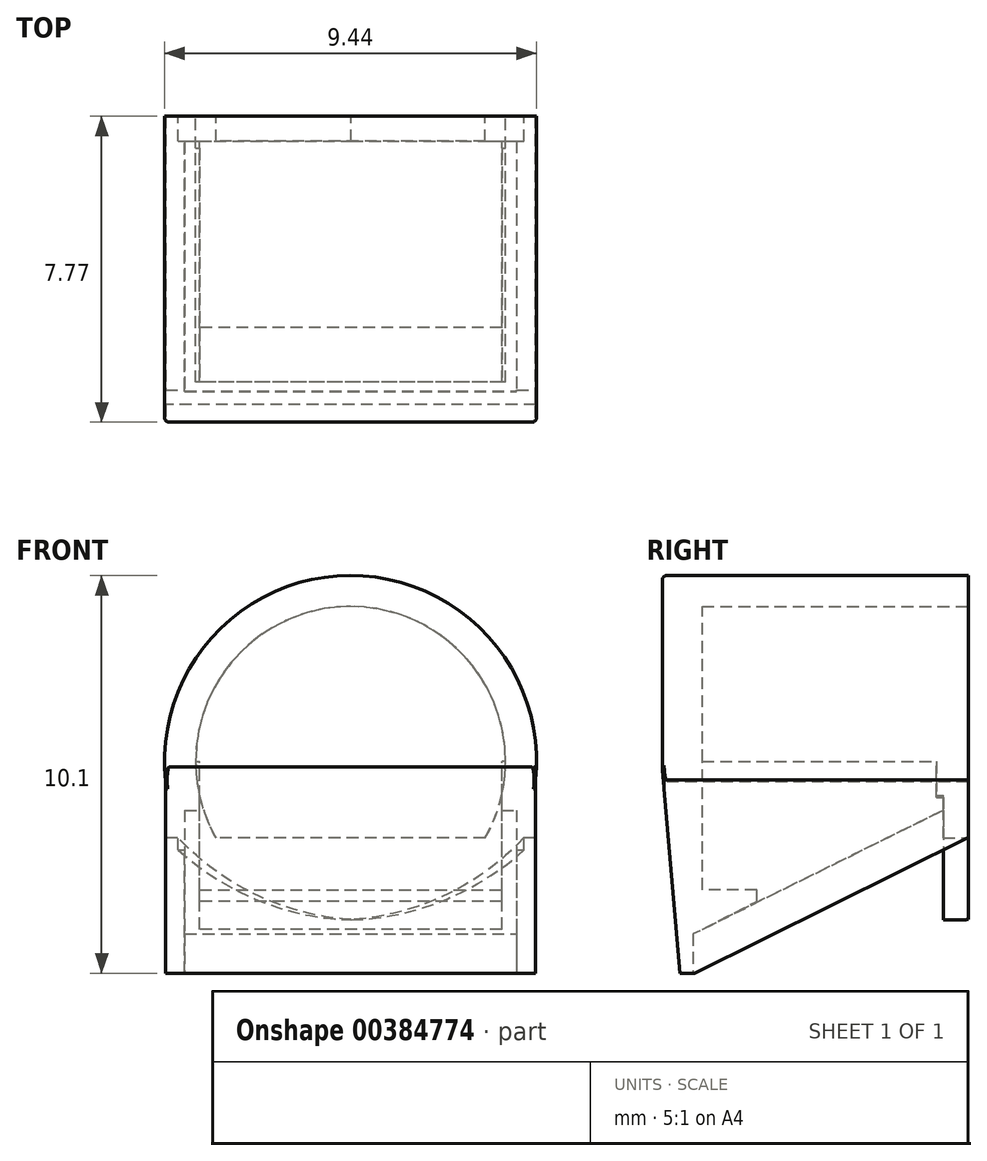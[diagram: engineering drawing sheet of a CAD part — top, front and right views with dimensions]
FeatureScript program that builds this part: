
annotation { "Feature Type Name" : "Feature", "Feature Type Description" : "" }
export const myFeature = defineFeature(function(context is Context, id is Id, definition is map)
    precondition{}
    {
        {
            var Q0;
            Q0=qCreatedBy(makeId("Front.planeOp"),FACE);
            var sketch = newSketch(context, id + "F0", { "sketchPlane" : qUnion([Q0])});
            skCircle(sketch, "E0", {"center": v(0, 0) * mm, "radius": 4.72 * mm});
            skSolve(sketch);
        }
        {
            var Q0;
            Q0=qCreatedBy(makeId("Front.planeOp"),FACE);
            var sketch = newSketch(context, id + "F1", { "sketchPlane" : qUnion([Q0])});
            skCircle(sketch, "E1", {"center": v(0, 0) * mm, "radius": 3.94 * mm});
            skSolve(sketch);
        }
        {
            var Q0;
            Q0=makeQuery(id+"F0.imprint","IMPRINT",FACE,{"disambiguationData":[TD([[makeQuery(id+"F0.imprint","IMPRINT",EDGE,{"derivedFrom":sQuery(id+"F0.wireOp",EDGE,"E0")}),1.0]])]});
            extrude(context, id + "F2", {"entities" : qUnion([Q0]), "depth" : 7.77 * mm});
        }
        {
            var Q0;
            Q0=makeQuery(id+"F1.imprint","IMPRINT",FACE,{"disambiguationData":[TD([[makeQuery(id+"F1.imprint","IMPRINT",EDGE,{"derivedFrom":sQuery(id+"F1.wireOp",EDGE,"E1")}),1.0]])]});
            extrude(context, id + "F3", {"entities" : qUnion([Q0]), "operationType" : NewBodyOperationType.REMOVE, "depth" : 6.76 * mm});
        }
        {
            var Q0;
            Q0=qCreatedBy(makeId("Top.planeOp"),FACE);
            var sketch = newSketch(context, id + "F4", { "sketchPlane" : qUnion([Q0])});
            skLineSegment(sketch, "E2.bottom", {"start": v(3.84, 0) * mm, "end": v(-3.83, 0) * mm});
            skLineSegment(sketch, "E2.top", {"start": v(3.84, -6.76) * mm, "end": v(-3.83, -6.76) * mm});
            skLineSegment(sketch, "E2.left", {"start": v(3.84, 0) * mm, "end": v(3.84, -6.76) * mm});
            skLineSegment(sketch, "E2.right", {"start": v(-3.83, 0) * mm, "end": v(-3.83, -6.76) * mm});
            skSolve(sketch);
        }
        {
            var Q0;
            Q0=qCreatedBy(makeId("Top.planeOp"),FACE);
            var sketch = newSketch(context, id + "F5", { "sketchPlane" : qUnion([Q0])});
            skLineSegment(sketch, "E3.bottom", {"start": v(-4.7, -7.73) * mm, "end": v(4.7, -7.73) * mm});
            skLineSegment(sketch, "E3.top", {"start": v(-4.7, 0) * mm, "end": v(4.7, 0) * mm});
            skLineSegment(sketch, "E3.left", {"start": v(-4.7, -7.73) * mm, "end": v(-4.7, 0) * mm});
            skLineSegment(sketch, "E3.right", {"start": v(4.7, -7.73) * mm, "end": v(4.7, 0) * mm});
            skSolve(sketch);
        }
        {
            var Q0;
            Q0=makeQuery(id+"F5.imprint","IMPRINT",FACE,{"disambiguationData":[TD([[makeQuery(id+"F5.imprint","IMPRINT",EDGE,{"derivedFrom":sQuery(id+"F5.wireOp",EDGE,"E3.bottom")}),1.0]])]});
            extrude(context, id + "F6", {"entities" : qUnion([Q0]), "operationType" : NewBodyOperationType.ADD, "oppositeDirection" : true, "depth" : 5.38 * mm});
        }
        {
            var Q0;
            Q0=makeQuery(id+"F4.imprint","IMPRINT",FACE,{"disambiguationData":[TD([[makeQuery(id+"F4.imprint","IMPRINT",EDGE,{"derivedFrom":sQuery(id+"F4.wireOp",EDGE,"E2.bottom")}),1.0]])]});
            extrude(context, id + "F7", {"entities" : qUnion([Q0]), "operationType" : NewBodyOperationType.REMOVE, "oppositeDirection" : true, "depth" : 11.68 * mm});
        }
        {
            var Q0;
            Q0=qCreatedBy(makeId("Right.planeOp"),FACE);
            var sketch = newSketch(context, id + "F8", { "sketchPlane" : qUnion([Q0])});
            skLineSegment(sketch, "E4", {"start": v(-7.57, -5.7) * mm, "end": v(0, -1.93) * mm});
            skLineSegment(sketch, "E5", {"start": v(0, -1.93) * mm, "end": v(0, -5.74) * mm});
            skLineSegment(sketch, "E6", {"start": v(0, -5.74) * mm, "end": v(-7.57, -5.7) * mm});
            skSolve(sketch);
        }
        {
            var Q0;
            Q0=makeQuery(id+"F8.imprint","IMPRINT",FACE,{"disambiguationData":[TD([[makeQuery(id+"F8.imprint","IMPRINT",EDGE,{"derivedFrom":sQuery(id+"F8.wireOp",EDGE,"E4")}),-1.0]])]});
            extrude(context, id + "F9", {"entities" : qUnion([Q0]), "operationType" : NewBodyOperationType.REMOVE, "endBound" : BoundingType.SYMMETRIC, "depth" : 25.4 * mm});
        }
        {
            var Q0;
            Q0=qCreatedBy(makeId("Right.planeOp"),FACE);
            var sketch = newSketch(context, id + "F10", { "sketchPlane" : qUnion([Q0])});
            skLineSegment(sketch, "E7", {"start": v(-7.32, -5.45) * mm, "end": v(-7.86, 0.92) * mm});
            skLineSegment(sketch, "E8", {"start": v(-7.86, 0.92) * mm, "end": v(-7.86, -5.5) * mm});
            skLineSegment(sketch, "E9", {"start": v(-7.86, -5.5) * mm, "end": v(-7.32, -5.45) * mm});
            skSolve(sketch);
        }
        {
            var Q0;
            Q0=makeQuery(id+"F10.imprint","IMPRINT",FACE,{"disambiguationData":[TD([[makeQuery(id+"F10.imprint","IMPRINT",EDGE,{"derivedFrom":sQuery(id+"F10.wireOp",EDGE,"E7")}),1.0]])]});
            extrude(context, id + "F11", {"entities" : qUnion([Q0]), "operationType" : NewBodyOperationType.REMOVE, "endBound" : BoundingType.SYMMETRIC, "oppositeDirection" : true, "depth" : 25.4 * mm});
        }
        {
            var Q0;
            Q0=qCreatedBy(makeId("Right.planeOp"),FACE);
            var sketch = newSketch(context, id + "F12", { "sketchPlane" : qUnion([Q0])});
            skLineSegment(sketch, "E10", {"start": v(-6.99, -5.4) * mm, "end": v(0, -1.94) * mm});
            skLineSegment(sketch, "E11", {"start": v(0, -1.94) * mm, "end": v(0, -0.93) * mm});
            skLineSegment(sketch, "E12", {"start": v(0, -0.93) * mm, "end": v(-6.99, -4.38) * mm});
            skLineSegment(sketch, "E13", {"start": v(-6.99, -4.38) * mm, "end": v(-6.99, -5.4) * mm});
            skSolve(sketch);
        }
        {
            var Q0;
            Q0=makeQuery(id+"F12.imprint","IMPRINT",FACE,{"disambiguationData":[TD([[makeQuery(id+"F12.imprint","IMPRINT",EDGE,{"derivedFrom":sQuery(id+"F12.wireOp",EDGE,"E10")}),1.0]])]});
            extrude(context, id + "F13", {"entities" : qUnion([Q0]), "operationType" : NewBodyOperationType.REMOVE, "endBound" : BoundingType.SYMMETRIC, "oppositeDirection" : true, "depth" : 8.43 * mm});
        }
        {
            var Q0;
            Q0=qCreatedBy(makeId("Right.planeOp"),FACE);
            var sketch = newSketch(context, id + "F14", { "sketchPlane" : qUnion([Q0])});
            skLineSegment(sketch, "E14", {"start": v(-6.99, -4.38) * mm, "end": v(-5.37, -3.56) * mm});
            skLineSegment(sketch, "E15", {"start": v(-5.37, -3.56) * mm, "end": v(-5.37, -3.26) * mm});
            skLineSegment(sketch, "E16", {"start": v(-5.37, -3.26) * mm, "end": v(-7.01, -3.26) * mm});
            skLineSegment(sketch, "E17", {"start": v(-7.01, -3.26) * mm, "end": v(-6.99, -4.38) * mm});
            skSolve(sketch);
        }
        {
            var Q0;
            Q0=makeQuery(id+"F14.imprint","IMPRINT",FACE,{"disambiguationData":[TD([[makeQuery(id+"F14.imprint","IMPRINT",EDGE,{"derivedFrom":sQuery(id+"F14.wireOp",EDGE,"E14")}),1.0]])]});
            extrude(context, id + "F15", {"entities" : qUnion([Q0]), "operationType" : NewBodyOperationType.ADD, "endBound" : BoundingType.SYMMETRIC, "depth" : 7.82 * mm});
        }
        {
            var Q0;
            Q0=makeQuery(id+"F2.opExtrude","CAP_EDGE",EDGE,{"disambiguationData":[OSD([sQuery(id+"F0.wireOp",EDGE,"E0")])],"isStart":false});
            fillet(context, id + "F16", {"entities" : qUnion([Q0]), "radius" : 0.12 * mm, "tangentPropagation" : true, "allowEdgeOverflow" : false});
        }
        {
            var Q0;
            Q0=qCreatedBy(makeId("Front.planeOp"),FACE);
            var sketch = newSketch(context, id + "F17", { "sketchPlane" : qUnion([Q0])});
            skLineSegment(sketch, "E18.bottom", {"start": v(4.4, 0) * mm, "end": v(-4.38, 0) * mm});
            skLineSegment(sketch, "E18.top", {"start": v(4.4, -4.03) * mm, "end": v(-4.38, -4.03) * mm});
            skLineSegment(sketch, "E18.left", {"start": v(4.4, 0) * mm, "end": v(4.4, -4.03) * mm});
            skLineSegment(sketch, "E18.right", {"start": v(-4.38, 0) * mm, "end": v(-4.38, -4.03) * mm});
            skSolve(sketch);
        }
        {
            var Q0;
            Q0=makeQuery(id+"F17.imprint","IMPRINT",FACE,{"disambiguationData":[TD([[makeQuery(id+"F17.imprint","IMPRINT",EDGE,{"derivedFrom":sQuery(id+"F17.wireOp",EDGE,"E18.bottom")}),1.0]])]});
            extrude(context, id + "F18", {"entities" : qUnion([Q0]), "operationType" : NewBodyOperationType.ADD, "depth" : 0.64 * mm});
        }
        {
            var Q0;
            Q0=qCreatedBy(makeId("Front.planeOp"),FACE);
            var sketch = newSketch(context, id + "F19", { "sketchPlane" : qUnion([Q0])});
            skCircle(sketch, "E19", {"center": v(0, 0) * mm, "radius": 3.94 * mm});
            skSolve(sketch);
        }
        {
            var Q0;
            Q0=makeQuery(id+"F19.imprint","IMPRINT",FACE,{"disambiguationData":[TD([[makeQuery(id+"F19.imprint","IMPRINT",EDGE,{"derivedFrom":sQuery(id+"F19.wireOp",EDGE,"E19")}),1.0]])]});
            extrude(context, id + "F20", {"entities" : qUnion([Q0]), "operationType" : NewBodyOperationType.REMOVE, "depth" : 0.81 * mm});
        }
        {
            var Q0;
            Q0=qCreatedBy(makeId("Front.planeOp"),FACE);
            var sketch = newSketch(context, id + "F21", { "sketchPlane" : qUnion([Q0])});
            skLineSegment(sketch, "E20", {"start": v(3.94, -1.95) * mm, "end": v(-3.77, -1.95) * mm});
            skLineSegment(sketch, "E21", {"start": v(-3.77, -1.95) * mm, "end": v(-1.68, -3.86) * mm});
            skLineSegment(sketch, "E22", {"start": v(-1.68, -3.86) * mm, "end": v(0, -3.97) * mm});
            skLineSegment(sketch, "E23", {"start": v(0, -3.97) * mm, "end": v(1.71, -3.94) * mm});
            skLineSegment(sketch, "E24", {"start": v(1.71, -3.94) * mm, "end": v(3.94, -1.95) * mm});
            skSolve(sketch);
        }
        {
            var Q0;
            Q0=makeQuery(id+"F21.imprint","IMPRINT",FACE,{"disambiguationData":[TD([[makeQuery(id+"F21.imprint","IMPRINT",EDGE,{"derivedFrom":sQuery(id+"F21.wireOp",EDGE,"E20")}),1.0]])]});
            extrude(context, id + "F22", {"entities" : qUnion([Q0]), "operationType" : NewBodyOperationType.ADD, "depth" : 0.64 * mm});
        }
        {
            var Q0;
            Q0=makeQuery(id+"F18.opExtrude","SWEPT_EDGE",EDGE,{"disambiguationData":[OSD([sQuery(id+"F17.wireOp",EDGE,"E18.top"),sQuery(id+"F17.wireOp",EDGE,"E18.right")])]});
            var Q1;
            Q1=makeQuery(id+"F18.opExtrude","SWEPT_EDGE",EDGE,{"disambiguationData":[OSD([sQuery(id+"F17.wireOp",EDGE,"E18.top"),sQuery(id+"F17.wireOp",EDGE,"E18.left")])]});
            fillet(context, id + "F23", {"entities" : qUnion([Q0, Q1]), "radius" : 5.89 * mm, "tangentPropagation" : true, "allowEdgeOverflow" : false});
        }
    });
